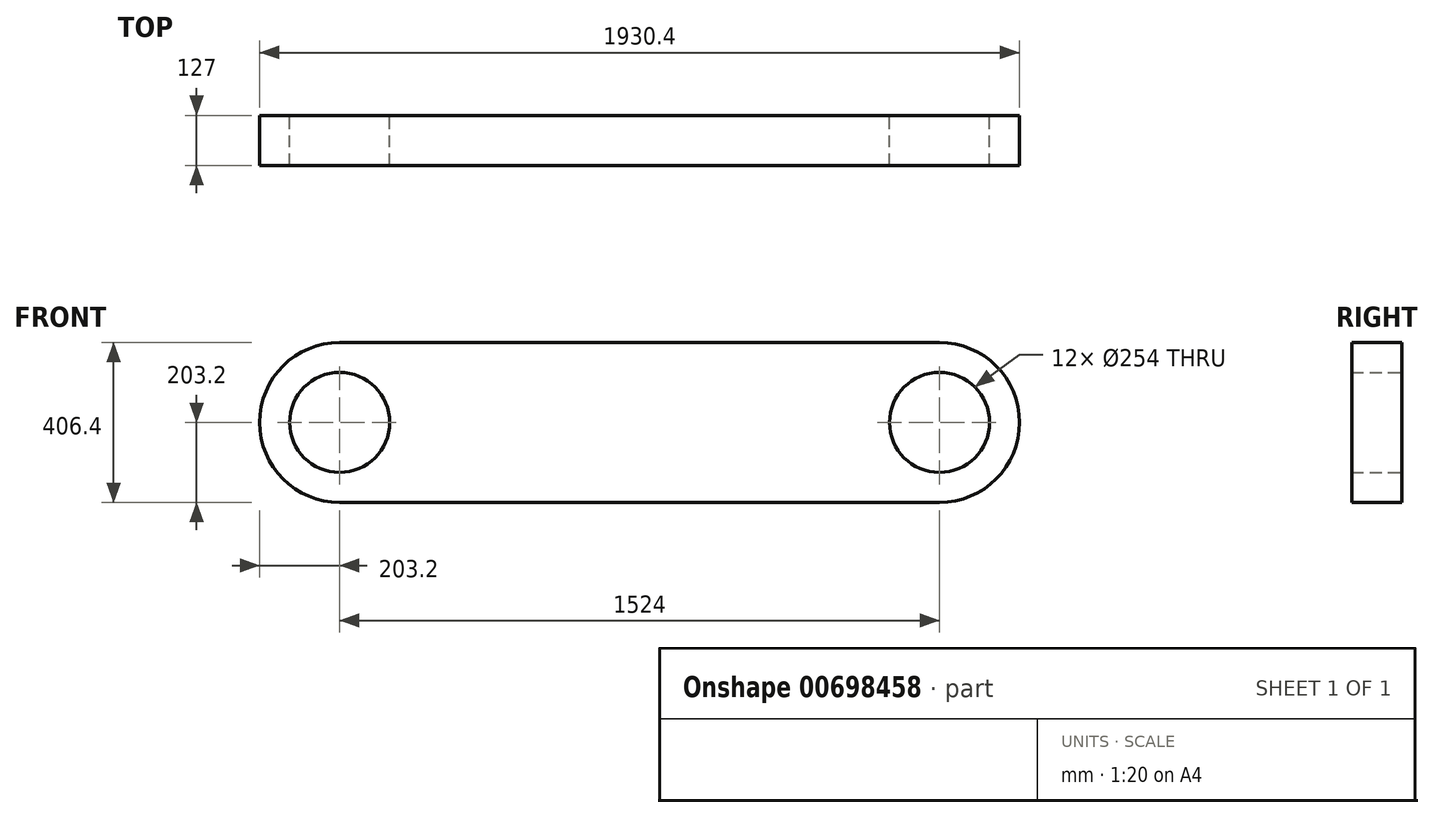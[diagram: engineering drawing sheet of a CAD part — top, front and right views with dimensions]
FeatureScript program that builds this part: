
annotation { "Feature Type Name" : "Feature", "Feature Type Description" : "" }
export const myFeature = defineFeature(function(context is Context, id is Id, definition is map)
    precondition{}
    {
        {
            var Q0;
            Q0=qCreatedBy(makeId("Front.planeOp"),FACE);
            var sketch = newSketch(context, id + "F0", { "sketchPlane" : qUnion([Q0])});
            skLineSegment(sketch, "E0.bottom", {"start": v(-762, 203.2) * mm, "end": v(762, 203.2) * mm});
            skLineSegment(sketch, "E0.top", {"start": v(-762, -203.2) * mm, "end": v(762, -203.2) * mm});
            skArc(sketch, "E1", {"start": v(-762, 203.2) * mm, "mid": v(-965.2, 0) * mm, "end": v(-762, -203.2) * mm});
            skArc(sketch, "E2", {"start": v(762, -203.2) * mm, "mid": v(965.2, 0) * mm, "end": v(762, 203.2) * mm});
            skCircle(sketch, "E3", {"center": v(-762, 0) * mm, "radius": 127 * mm});
            skCircle(sketch, "E4", {"center": v(762, 0) * mm, "radius": 127 * mm});
            skSolve(sketch);
        }
        {
            var Q0;
            Q0=qSketchRegion(id+"F0",true);
            extrude(context, id + "F1", {"entities" : qUnion([Q0]), "endBound" : BoundingType.SYMMETRIC, "depth" : 127 * mm, "offsetDistance" : 25.4 * mm});
        }
    });
